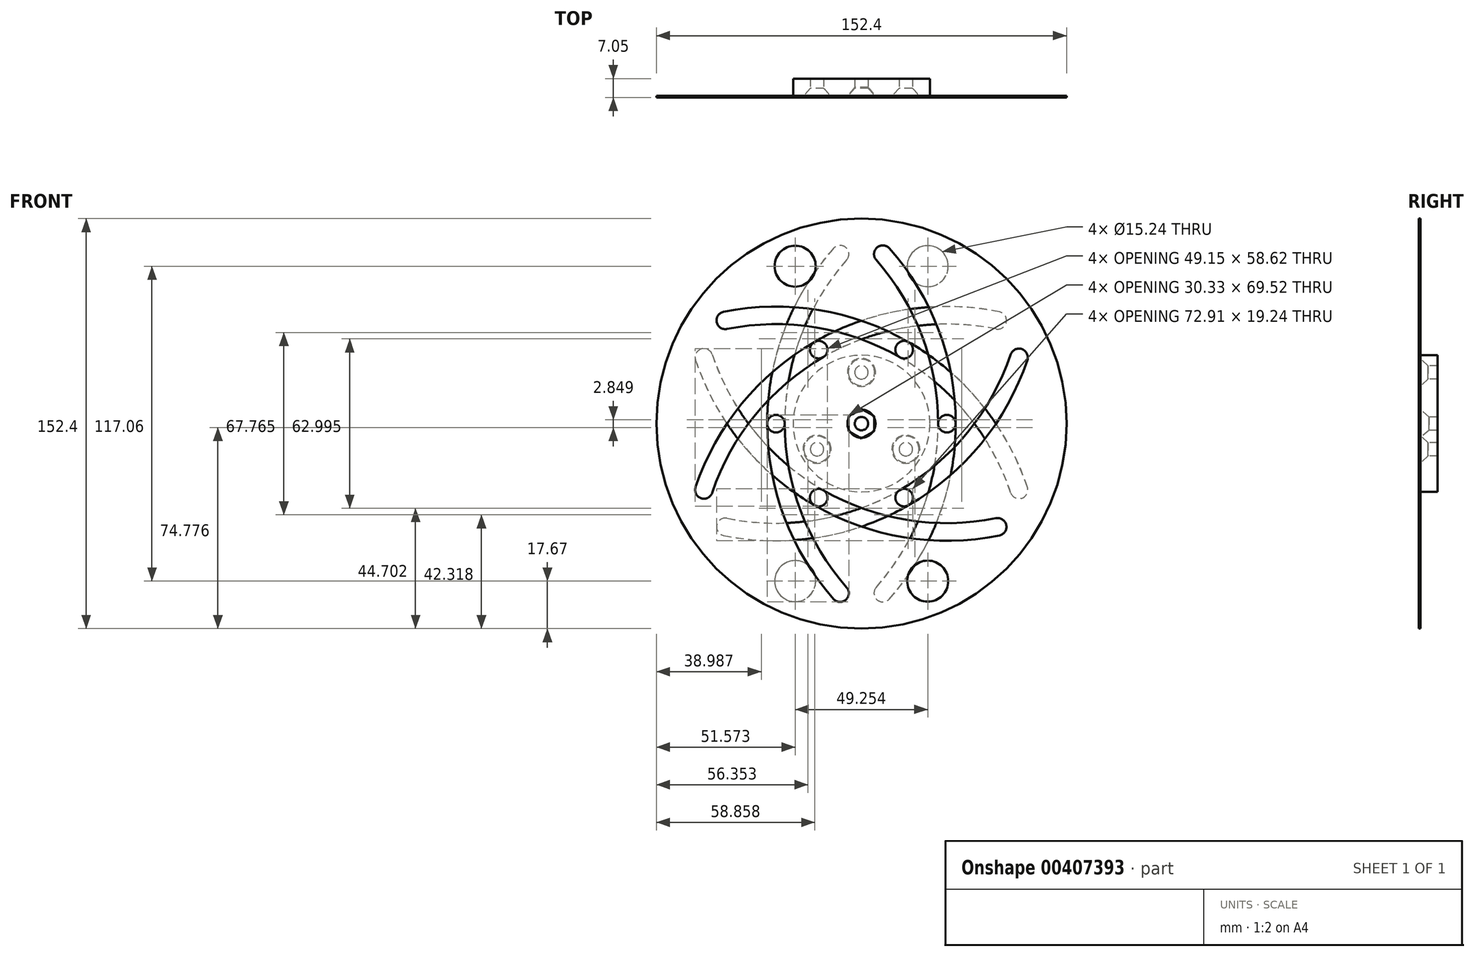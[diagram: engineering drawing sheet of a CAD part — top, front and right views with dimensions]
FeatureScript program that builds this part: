
annotation { "Feature Type Name" : "Feature", "Feature Type Description" : "" }
export const myFeature = defineFeature(function(context is Context, id is Id, definition is map)
    precondition{}
    {
        {
            assignVariable(context, id + "F0", {"name" : "plateThickness", "anyValue" : 0.35});
        }
        {
            var Q0;
            Q0=qCreatedBy(makeId("Front.planeOp"),FACE);
            var sketch = newSketch(context, id + "F1", { "sketchPlane" : qUnion([Q0])});
            skCircle(sketch, "E0", {"center": v(0, 0) * mm, "radius": 76.2 * mm});
            skLineSegment(sketch, "E1", {"start": v(38.1, -66) * mm, "end": v(-38.1, 66) * mm, "construction": true});
            skLineSegment(sketch, "E2", {"start": v(-76.2, 0) * mm, "end": v(76.2, 0) * mm, "construction": true});
            skCircle(sketch, "E3", {"center": v(0, 0) * mm, "radius": 63.5 * mm, "construction": true});
            skCircle(sketch, "E4", {"center": v(0, 0) * mm, "radius": 31.75 * mm, "construction": true});
            skLineSegment(sketch, "E5", {"start": v(27.7, -15.53) * mm, "end": v(55.38, -31.06) * mm, "construction": true});
            skPoint(sketch, "E6", {"position": v(41.54, -23.3) * mm});
            skArc(sketch, "E7", {"start": v(58.53, 24.63) * mm, "mid": v(41.96, -5.33) * mm, "end": v(15.87, -27.5) * mm, "construction": true});
            skArc(sketch, "E8.0.startCap", {"start": v(55.44, 25.67) * mm, "mid": v(59.57, 27.72) * mm, "end": v(61.62, 23.59) * mm});
            skArc(sketch, "E8.0.endCap", {"start": v(17.5, -30.32) * mm, "mid": v(13.05, -29.13) * mm, "end": v(14.24, -24.67) * mm});
            skArc(sketch, "E8.0.left", {"start": v(61.62, 23.59) * mm, "mid": v(44.49, -7.4) * mm, "end": v(17.5, -30.32) * mm});
            skArc(sketch, "E8.0.right", {"start": v(55.44, 25.67) * mm, "mid": v(39.44, -3.26) * mm, "end": v(14.24, -24.67) * mm});
            skLineSegment(sketch, "E9", {"start": v(0, 0) * mm, "end": v(0, 76.2) * mm, "construction": true});
            skArc(sketch, "E10.1.0", {"start": v(10.39, 65.16) * mm, "mid": v(28.65, 34.83) * mm, "end": v(35.01, 0) * mm});
            skArc(sketch, "E10.1.1", {"start": v(5.49, 60.84) * mm, "mid": v(22.55, 32.52) * mm, "end": v(28.49, 0) * mm});
            skArc(sketch, "E10.1.2", {"start": v(35.01, 0) * mm, "mid": v(31.75, -3.26) * mm, "end": v(28.49, 0) * mm});
            skArc(sketch, "E10.1.3", {"start": v(5.49, 60.84) * mm, "mid": v(5.78, 65.45) * mm, "end": v(10.39, 65.16) * mm});
            skArc(sketch, "E10.2.0", {"start": v(-51.24, 41.57) * mm, "mid": v(-15.84, 42.23) * mm, "end": v(17.5, 30.32) * mm});
            skArc(sketch, "E10.2.1", {"start": v(-49.95, 35.18) * mm, "mid": v(-16.9, 35.79) * mm, "end": v(14.24, 24.67) * mm});
            skArc(sketch, "E10.2.2", {"start": v(17.5, 30.32) * mm, "mid": v(18.7, 25.86) * mm, "end": v(14.24, 24.67) * mm});
            skArc(sketch, "E10.2.3", {"start": v(-49.95, 35.18) * mm, "mid": v(-53.8, 37.73) * mm, "end": v(-51.24, 41.57) * mm});
            skArc(sketch, "E11.3.3.0", {"start": v(-61.62, -23.59) * mm, "mid": v(-44.49, 7.4) * mm, "end": v(-17.5, 30.32) * mm});
            skArc(sketch, "E11.4.3.0", {"start": v(-55.44, -25.67) * mm, "mid": v(-39.44, 3.26) * mm, "end": v(-14.24, 24.67) * mm});
            skArc(sketch, "E11.8.3.0", {"start": v(-17.5, 30.32) * mm, "mid": v(-13.05, 29.13) * mm, "end": v(-14.24, 24.67) * mm});
            skArc(sketch, "E11.12.3.0", {"start": v(-55.44, -25.67) * mm, "mid": v(-59.57, -27.72) * mm, "end": v(-61.62, -23.59) * mm});
            skArc(sketch, "E11.3.4.0", {"start": v(-10.39, -65.16) * mm, "mid": v(-28.65, -34.83) * mm, "end": v(-35.01, 0) * mm});
            skArc(sketch, "E11.4.4.0", {"start": v(-5.49, -60.84) * mm, "mid": v(-22.55, -32.52) * mm, "end": v(-28.49, 0) * mm});
            skArc(sketch, "E11.8.4.0", {"start": v(-35.01, 0) * mm, "mid": v(-31.75, 3.26) * mm, "end": v(-28.49, 0) * mm});
            skArc(sketch, "E11.12.4.0", {"start": v(-5.49, -60.84) * mm, "mid": v(-5.78, -65.45) * mm, "end": v(-10.39, -65.16) * mm});
            skArc(sketch, "E11.3.5.0", {"start": v(51.24, -41.57) * mm, "mid": v(15.84, -42.23) * mm, "end": v(-17.5, -30.32) * mm});
            skArc(sketch, "E11.4.5.0", {"start": v(49.95, -35.18) * mm, "mid": v(16.9, -35.79) * mm, "end": v(-14.24, -24.67) * mm});
            skArc(sketch, "E11.8.5.0", {"start": v(-17.5, -30.32) * mm, "mid": v(-18.7, -25.86) * mm, "end": v(-14.24, -24.67) * mm});
            skArc(sketch, "E11.12.5.0", {"start": v(49.95, -35.18) * mm, "mid": v(53.8, -37.73) * mm, "end": v(51.24, -41.57) * mm});
            skCircle(sketch, "E12", {"center": v(-24.63, 58.53) * mm, "radius": 7.62 * mm});
            skArc(sketch, "E13", {"start": v(7.94, 63) * mm, "mid": v(-24.63, 58.53) * mm, "end": v(-50.6, 38.38) * mm, "construction": true});
            skCircle(sketch, "E14.1.0", {"center": v(24.63, -58.53) * mm, "radius": 7.62 * mm});
            skSolve(sketch);
        }
        {
            var Q0;
            Q0=qSketchRegion(id+"F1",true);
            var Q1;
            Q1=makeQuery(id+"F1.imprint","IMPRINT",FACE,{"disambiguationData":[TD([[makeQuery(id+"F1.imprint","IMPRINT",EDGE,{"derivedFrom":sQuery(id+"F1.wireOp",EDGE,"b587f6b5-7a6a-44af-b427-4ee7b0e66231.0")}),1.0]])]});
            var Q2;
            Q2=makeQuery(id+"F1.imprint","IMPRINT",FACE,{"disambiguationData":[TD([[makeQuery(id+"F1.imprint","IMPRINT",EDGE,{"derivedFrom":sQuery(id+"F1.wireOp",EDGE,"vc4YVOHs-SVUY-lYLu-5kIK-RnGjNBiSBPxz")}),-1.0]])]});
            extrude(context, id + "F2", {"entities" : qUnion([Q0, Q1, Q2]), "depth" : (getVariable(context, 'plateThickness')) * mm, "offsetDistance" : 25.4 * mm});
        }
        {
            var Q0;
            Q0=makeQuery(id+"F1.imprint","IMPRINT",FACE,{"disambiguationData":[TD([[makeQuery(id+"F1.imprint","IMPRINT",EDGE,{"derivedFrom":sQuery(id+"F1.wireOp",EDGE,"E0")}),1.0]])]});
            var Q1;
            Q1=makeQuery(id+"F2.opExtrude","CAP_FACE",FACE,{"disambiguationData":[OSD([sQuery(id+"F1.wireOp",EDGE,"E0"),sQuery(id+"F1.wireOp",EDGE,"E8.0.startCap"),sQuery(id+"F1.wireOp",EDGE,"E8.0.endCap"),sQuery(id+"F1.wireOp",EDGE,"E8.0.left"),sQuery(id+"F1.wireOp",EDGE,"E8.0.right"),sQuery(id+"F1.wireOp",EDGE,"9beebe2f-deec-4e0b-bc73-9199ee26bee9.1.0"),sQuery(id+"F1.wireOp",EDGE,"9beebe2f-deec-4e0b-bc73-9199ee26bee9.1.1"),sQuery(id+"F1.wireOp",EDGE,"9beebe2f-deec-4e0b-bc73-9199ee26bee9.1.2"),sQuery(id+"F1.wireOp",EDGE,"9beebe2f-deec-4e0b-bc73-9199ee26bee9.1.3"),sQuery(id+"F1.wireOp",EDGE,"9beebe2f-deec-4e0b-bc73-9199ee26bee9.2.0"),sQuery(id+"F1.wireOp",EDGE,"9beebe2f-deec-4e0b-bc73-9199ee26bee9.2.1"),sQuery(id+"F1.wireOp",EDGE,"9beebe2f-deec-4e0b-bc73-9199ee26bee9.2.2"),sQuery(id+"F1.wireOp",EDGE,"9beebe2f-deec-4e0b-bc73-9199ee26bee9.2.3"),sQuery(id+"F1.wireOp",EDGE,"9beebe2f-deec-4e0b-bc73-9199ee26bee9.3.0"),sQuery(id+"F1.wireOp",EDGE,"9beebe2f-deec-4e0b-bc73-9199ee26bee9.3.1"),sQuery(id+"F1.wireOp",EDGE,"9beebe2f-deec-4e0b-bc73-9199ee26bee9.3.2"),sQuery(id+"F1.wireOp",EDGE,"9beebe2f-deec-4e0b-bc73-9199ee26bee9.3.3"),sQuery(id+"F1.wireOp",EDGE,"9beebe2f-deec-4e0b-bc73-9199ee26bee9.4.0"),sQuery(id+"F1.wireOp",EDGE,"9beebe2f-deec-4e0b-bc73-9199ee26bee9.4.1"),sQuery(id+"F1.wireOp",EDGE,"9beebe2f-deec-4e0b-bc73-9199ee26bee9.4.2"),sQuery(id+"F1.wireOp",EDGE,"9beebe2f-deec-4e0b-bc73-9199ee26bee9.4.3"),sQuery(id+"F1.wireOp",EDGE,"9beebe2f-deec-4e0b-bc73-9199ee26bee9.5.0"),sQuery(id+"F1.wireOp",EDGE,"9beebe2f-deec-4e0b-bc73-9199ee26bee9.5.1"),sQuery(id+"F1.wireOp",EDGE,"9beebe2f-deec-4e0b-bc73-9199ee26bee9.5.2"),sQuery(id+"F1.wireOp",EDGE,"9beebe2f-deec-4e0b-bc73-9199ee26bee9.5.3"),sQuery(id+"F1.wireOp",EDGE,"b587f6b5-7a6a-44af-b427-4ee7b0e66231.0"),sQuery(id+"F1.wireOp",EDGE,"b587f6b5-7a6a-44af-b427-4ee7b0e66231.1"),sQuery(id+"F1.wireOp",EDGE,"b587f6b5-7a6a-44af-b427-4ee7b0e66231.2"),sQuery(id+"F1.wireOp",EDGE,"b587f6b5-7a6a-44af-b427-4ee7b0e66231.3"),sQuery(id+"F1.wireOp",EDGE,"b587f6b5-7a6a-44af-b427-4ee7b0e66231.4"),sQuery(id+"F1.wireOp",EDGE,"b587f6b5-7a6a-44af-b427-4ee7b0e66231.5")])],"isStart":false});
            extrude(context, id + "F3", {"entities" : qUnion([Q0]), "endBound" : BoundingType.UP_TO_SURFACE, "endBoundEntityFace" : qUnion([Q1]), "depth" : 25.4 * mm});
        }
        {
            var Q0;
            Q0=makeQuery(id+"F3.opExtrude","SWEPT_BODY",BODY,{"disambiguationData":[OSD([sQuery(id+"F1.wireOp",EDGE,"E0"),sQuery(id+"F1.wireOp",EDGE,"E8.0.startCap"),sQuery(id+"F1.wireOp",EDGE,"E8.0.endCap"),sQuery(id+"F1.wireOp",EDGE,"E8.0.left"),sQuery(id+"F1.wireOp",EDGE,"E8.0.right"),sQuery(id+"F1.wireOp",EDGE,"9beebe2f-deec-4e0b-bc73-9199ee26bee9.1.0"),sQuery(id+"F1.wireOp",EDGE,"9beebe2f-deec-4e0b-bc73-9199ee26bee9.1.1"),sQuery(id+"F1.wireOp",EDGE,"9beebe2f-deec-4e0b-bc73-9199ee26bee9.1.2"),sQuery(id+"F1.wireOp",EDGE,"9beebe2f-deec-4e0b-bc73-9199ee26bee9.1.3"),sQuery(id+"F1.wireOp",EDGE,"9beebe2f-deec-4e0b-bc73-9199ee26bee9.2.0"),sQuery(id+"F1.wireOp",EDGE,"9beebe2f-deec-4e0b-bc73-9199ee26bee9.2.1"),sQuery(id+"F1.wireOp",EDGE,"9beebe2f-deec-4e0b-bc73-9199ee26bee9.2.2"),sQuery(id+"F1.wireOp",EDGE,"9beebe2f-deec-4e0b-bc73-9199ee26bee9.2.3"),sQuery(id+"F1.wireOp",EDGE,"9beebe2f-deec-4e0b-bc73-9199ee26bee9.3.0"),sQuery(id+"F1.wireOp",EDGE,"9beebe2f-deec-4e0b-bc73-9199ee26bee9.3.1"),sQuery(id+"F1.wireOp",EDGE,"9beebe2f-deec-4e0b-bc73-9199ee26bee9.3.2"),sQuery(id+"F1.wireOp",EDGE,"9beebe2f-deec-4e0b-bc73-9199ee26bee9.3.3"),sQuery(id+"F1.wireOp",EDGE,"9beebe2f-deec-4e0b-bc73-9199ee26bee9.4.0"),sQuery(id+"F1.wireOp",EDGE,"9beebe2f-deec-4e0b-bc73-9199ee26bee9.4.1"),sQuery(id+"F1.wireOp",EDGE,"9beebe2f-deec-4e0b-bc73-9199ee26bee9.4.2"),sQuery(id+"F1.wireOp",EDGE,"9beebe2f-deec-4e0b-bc73-9199ee26bee9.4.3"),sQuery(id+"F1.wireOp",EDGE,"9beebe2f-deec-4e0b-bc73-9199ee26bee9.5.0"),sQuery(id+"F1.wireOp",EDGE,"9beebe2f-deec-4e0b-bc73-9199ee26bee9.5.1"),sQuery(id+"F1.wireOp",EDGE,"9beebe2f-deec-4e0b-bc73-9199ee26bee9.5.2"),sQuery(id+"F1.wireOp",EDGE,"9beebe2f-deec-4e0b-bc73-9199ee26bee9.5.3"),sQuery(id+"F1.wireOp",EDGE,"bZYdzHVk-sqhN-pvqg-Ma4H-s01bYcmrYiZ1")])]});
            var Q1;
            Q1=sQuery(id+"F1.wireOp",EDGE,"E9");
            transform(context, id + "F4", {"entities" : qUnion([Q0]), "transformType" : TransformType.ROTATION, "transformAxis" : qUnion([Q1]), "angle" : 180 * degree, "makeCopy" : false});
        }
        {
            var Q0;
            Q0=makeQuery(id+"F2.opExtrude","CAP_FACE",FACE,{"disambiguationData":[OSD([sQuery(id+"F1.wireOp",EDGE,"E0"),sQuery(id+"F1.wireOp",EDGE,"E8.0.startCap"),sQuery(id+"F1.wireOp",EDGE,"E8.0.endCap"),sQuery(id+"F1.wireOp",EDGE,"E8.0.left"),sQuery(id+"F1.wireOp",EDGE,"E8.0.right"),sQuery(id+"F1.wireOp",EDGE,"9beebe2f-deec-4e0b-bc73-9199ee26bee9.1.0"),sQuery(id+"F1.wireOp",EDGE,"9beebe2f-deec-4e0b-bc73-9199ee26bee9.1.1"),sQuery(id+"F1.wireOp",EDGE,"9beebe2f-deec-4e0b-bc73-9199ee26bee9.1.2"),sQuery(id+"F1.wireOp",EDGE,"9beebe2f-deec-4e0b-bc73-9199ee26bee9.1.3"),sQuery(id+"F1.wireOp",EDGE,"9beebe2f-deec-4e0b-bc73-9199ee26bee9.2.0"),sQuery(id+"F1.wireOp",EDGE,"9beebe2f-deec-4e0b-bc73-9199ee26bee9.2.1"),sQuery(id+"F1.wireOp",EDGE,"9beebe2f-deec-4e0b-bc73-9199ee26bee9.2.2"),sQuery(id+"F1.wireOp",EDGE,"9beebe2f-deec-4e0b-bc73-9199ee26bee9.2.3"),sQuery(id+"F1.wireOp",EDGE,"9beebe2f-deec-4e0b-bc73-9199ee26bee9.3.0"),sQuery(id+"F1.wireOp",EDGE,"9beebe2f-deec-4e0b-bc73-9199ee26bee9.3.1"),sQuery(id+"F1.wireOp",EDGE,"9beebe2f-deec-4e0b-bc73-9199ee26bee9.3.2"),sQuery(id+"F1.wireOp",EDGE,"9beebe2f-deec-4e0b-bc73-9199ee26bee9.3.3"),sQuery(id+"F1.wireOp",EDGE,"9beebe2f-deec-4e0b-bc73-9199ee26bee9.4.0"),sQuery(id+"F1.wireOp",EDGE,"9beebe2f-deec-4e0b-bc73-9199ee26bee9.4.1"),sQuery(id+"F1.wireOp",EDGE,"9beebe2f-deec-4e0b-bc73-9199ee26bee9.4.2"),sQuery(id+"F1.wireOp",EDGE,"9beebe2f-deec-4e0b-bc73-9199ee26bee9.4.3"),sQuery(id+"F1.wireOp",EDGE,"9beebe2f-deec-4e0b-bc73-9199ee26bee9.5.0"),sQuery(id+"F1.wireOp",EDGE,"9beebe2f-deec-4e0b-bc73-9199ee26bee9.5.1"),sQuery(id+"F1.wireOp",EDGE,"9beebe2f-deec-4e0b-bc73-9199ee26bee9.5.2"),sQuery(id+"F1.wireOp",EDGE,"9beebe2f-deec-4e0b-bc73-9199ee26bee9.5.3")])],"isStart":false});
            var sketch = newSketch(context, id + "F5", { "sketchPlane" : qUnion([Q0])});
            skPoint(sketch, "E15", {"position": v(0, 0) * mm});
            skSolve(sketch);
        }
        {
            var Q0;
            Q0=sQuery(id+"F5.wireOp",VERTEX,"E15");
            var Q1;
            Q1=makeQuery(id+"F2.opExtrude","SWEPT_BODY",BODY,{"disambiguationData":[OSD([sQuery(id+"F1.wireOp",EDGE,"E0"),sQuery(id+"F1.wireOp",EDGE,"E8.0.startCap"),sQuery(id+"F1.wireOp",EDGE,"E8.0.endCap"),sQuery(id+"F1.wireOp",EDGE,"E8.0.left"),sQuery(id+"F1.wireOp",EDGE,"E8.0.right"),sQuery(id+"F1.wireOp",EDGE,"9beebe2f-deec-4e0b-bc73-9199ee26bee9.1.0"),sQuery(id+"F1.wireOp",EDGE,"9beebe2f-deec-4e0b-bc73-9199ee26bee9.1.1"),sQuery(id+"F1.wireOp",EDGE,"9beebe2f-deec-4e0b-bc73-9199ee26bee9.1.2"),sQuery(id+"F1.wireOp",EDGE,"9beebe2f-deec-4e0b-bc73-9199ee26bee9.1.3"),sQuery(id+"F1.wireOp",EDGE,"9beebe2f-deec-4e0b-bc73-9199ee26bee9.2.0"),sQuery(id+"F1.wireOp",EDGE,"9beebe2f-deec-4e0b-bc73-9199ee26bee9.2.1"),sQuery(id+"F1.wireOp",EDGE,"9beebe2f-deec-4e0b-bc73-9199ee26bee9.2.2"),sQuery(id+"F1.wireOp",EDGE,"9beebe2f-deec-4e0b-bc73-9199ee26bee9.2.3"),sQuery(id+"F1.wireOp",EDGE,"9beebe2f-deec-4e0b-bc73-9199ee26bee9.3.0"),sQuery(id+"F1.wireOp",EDGE,"9beebe2f-deec-4e0b-bc73-9199ee26bee9.3.1"),sQuery(id+"F1.wireOp",EDGE,"9beebe2f-deec-4e0b-bc73-9199ee26bee9.3.2"),sQuery(id+"F1.wireOp",EDGE,"9beebe2f-deec-4e0b-bc73-9199ee26bee9.3.3"),sQuery(id+"F1.wireOp",EDGE,"9beebe2f-deec-4e0b-bc73-9199ee26bee9.4.0"),sQuery(id+"F1.wireOp",EDGE,"9beebe2f-deec-4e0b-bc73-9199ee26bee9.4.1"),sQuery(id+"F1.wireOp",EDGE,"9beebe2f-deec-4e0b-bc73-9199ee26bee9.4.2"),sQuery(id+"F1.wireOp",EDGE,"9beebe2f-deec-4e0b-bc73-9199ee26bee9.4.3"),sQuery(id+"F1.wireOp",EDGE,"9beebe2f-deec-4e0b-bc73-9199ee26bee9.5.0"),sQuery(id+"F1.wireOp",EDGE,"9beebe2f-deec-4e0b-bc73-9199ee26bee9.5.1"),sQuery(id+"F1.wireOp",EDGE,"9beebe2f-deec-4e0b-bc73-9199ee26bee9.5.2"),sQuery(id+"F1.wireOp",EDGE,"9beebe2f-deec-4e0b-bc73-9199ee26bee9.5.3")])]});
            hole(context, id + "F6", {"style" : HoleStyle.C_SINK, "endStyle" : HoleEndStyle.THROUGH, "standardTappedOrClearance" : lookupTablePath({ "standard" : "ANSI", "fit" : "Close", "size" : "#10", "type" : "Clearance" }), "standardBlindInLast" : lookupTablePath({ "fit" : "Close", "standard" : "ANSI", "size" : "#10", "type" : "Clearance" }), "holeDiameter" : 4.98 * mm, "cSinkDiameter" : 10.44 * mm, "cSinkAngle" : 82 * degree, "isTappedThrough" : true, "tappedDepth" : 12.7 * mm, "tapClearance" : 3, "locations" : qUnion([Q0]), "scope" : qUnion([Q1])});
        }
        {
            var Q0;
            Q0=sQuery(id+"F1.wireOp",VERTEX,"E0.center");
            var Q1;
            Q1=makeQuery(id+"F3.opExtrude","SWEPT_BODY",BODY,{"disambiguationData":[OSD([sQuery(id+"F1.wireOp",EDGE,"E0"),sQuery(id+"F1.wireOp",EDGE,"E8.0.startCap"),sQuery(id+"F1.wireOp",EDGE,"E8.0.endCap"),sQuery(id+"F1.wireOp",EDGE,"E8.0.left"),sQuery(id+"F1.wireOp",EDGE,"E8.0.right"),sQuery(id+"F1.wireOp",EDGE,"9beebe2f-deec-4e0b-bc73-9199ee26bee9.1.0"),sQuery(id+"F1.wireOp",EDGE,"9beebe2f-deec-4e0b-bc73-9199ee26bee9.1.1"),sQuery(id+"F1.wireOp",EDGE,"9beebe2f-deec-4e0b-bc73-9199ee26bee9.1.2"),sQuery(id+"F1.wireOp",EDGE,"9beebe2f-deec-4e0b-bc73-9199ee26bee9.1.3"),sQuery(id+"F1.wireOp",EDGE,"9beebe2f-deec-4e0b-bc73-9199ee26bee9.2.0"),sQuery(id+"F1.wireOp",EDGE,"9beebe2f-deec-4e0b-bc73-9199ee26bee9.2.1"),sQuery(id+"F1.wireOp",EDGE,"9beebe2f-deec-4e0b-bc73-9199ee26bee9.2.2"),sQuery(id+"F1.wireOp",EDGE,"9beebe2f-deec-4e0b-bc73-9199ee26bee9.2.3"),sQuery(id+"F1.wireOp",EDGE,"9beebe2f-deec-4e0b-bc73-9199ee26bee9.3.0"),sQuery(id+"F1.wireOp",EDGE,"9beebe2f-deec-4e0b-bc73-9199ee26bee9.3.1"),sQuery(id+"F1.wireOp",EDGE,"9beebe2f-deec-4e0b-bc73-9199ee26bee9.3.2"),sQuery(id+"F1.wireOp",EDGE,"9beebe2f-deec-4e0b-bc73-9199ee26bee9.3.3"),sQuery(id+"F1.wireOp",EDGE,"9beebe2f-deec-4e0b-bc73-9199ee26bee9.4.0"),sQuery(id+"F1.wireOp",EDGE,"9beebe2f-deec-4e0b-bc73-9199ee26bee9.4.1"),sQuery(id+"F1.wireOp",EDGE,"9beebe2f-deec-4e0b-bc73-9199ee26bee9.4.2"),sQuery(id+"F1.wireOp",EDGE,"9beebe2f-deec-4e0b-bc73-9199ee26bee9.4.3"),sQuery(id+"F1.wireOp",EDGE,"9beebe2f-deec-4e0b-bc73-9199ee26bee9.5.0"),sQuery(id+"F1.wireOp",EDGE,"9beebe2f-deec-4e0b-bc73-9199ee26bee9.5.1"),sQuery(id+"F1.wireOp",EDGE,"9beebe2f-deec-4e0b-bc73-9199ee26bee9.5.2"),sQuery(id+"F1.wireOp",EDGE,"9beebe2f-deec-4e0b-bc73-9199ee26bee9.5.3")])]});
            hole(context, id + "F7", {"style" : HoleStyle.SIMPLE, "endStyle" : HoleEndStyle.THROUGH, "standardTappedOrClearance" : lookupTablePath({ "standard" : "ANSI", "engagement" : "75%", "pitch" : "32 tpi", "size" : "#10", "type" : "Tapped" }), "standardBlindInLast" : lookupTablePath({ "standard" : "ANSI", "engagement" : "75%", "pitch" : "32 tpi", "size" : "#10", "type" : "Tapped" }), "holeDiameter" : 4.04 * mm, "showTappedDepth" : true, "isTappedThrough" : true, "tappedDepth" : 12.7 * mm, "tapClearance" : 3, "locations" : qUnion([Q0]), "scope" : qUnion([Q1]), "majorDiameter" : 4.83 * mm});
        }
        {
            var Q0;
            Q0=makeQuery(id+"F3.opExtrude","CAP_FACE",FACE,{"disambiguationData":[OSD([sQuery(id+"F1.wireOp",EDGE,"E0"),sQuery(id+"F1.wireOp",EDGE,"E8.0.startCap"),sQuery(id+"F1.wireOp",EDGE,"E8.0.endCap"),sQuery(id+"F1.wireOp",EDGE,"E8.0.left"),sQuery(id+"F1.wireOp",EDGE,"E8.0.right"),sQuery(id+"F1.wireOp",EDGE,"9beebe2f-deec-4e0b-bc73-9199ee26bee9.1.0"),sQuery(id+"F1.wireOp",EDGE,"9beebe2f-deec-4e0b-bc73-9199ee26bee9.1.1"),sQuery(id+"F1.wireOp",EDGE,"9beebe2f-deec-4e0b-bc73-9199ee26bee9.1.2"),sQuery(id+"F1.wireOp",EDGE,"9beebe2f-deec-4e0b-bc73-9199ee26bee9.1.3"),sQuery(id+"F1.wireOp",EDGE,"9beebe2f-deec-4e0b-bc73-9199ee26bee9.2.0"),sQuery(id+"F1.wireOp",EDGE,"9beebe2f-deec-4e0b-bc73-9199ee26bee9.2.1"),sQuery(id+"F1.wireOp",EDGE,"9beebe2f-deec-4e0b-bc73-9199ee26bee9.2.2"),sQuery(id+"F1.wireOp",EDGE,"9beebe2f-deec-4e0b-bc73-9199ee26bee9.2.3"),sQuery(id+"F1.wireOp",EDGE,"9beebe2f-deec-4e0b-bc73-9199ee26bee9.3.0"),sQuery(id+"F1.wireOp",EDGE,"9beebe2f-deec-4e0b-bc73-9199ee26bee9.3.1"),sQuery(id+"F1.wireOp",EDGE,"9beebe2f-deec-4e0b-bc73-9199ee26bee9.3.2"),sQuery(id+"F1.wireOp",EDGE,"9beebe2f-deec-4e0b-bc73-9199ee26bee9.3.3"),sQuery(id+"F1.wireOp",EDGE,"9beebe2f-deec-4e0b-bc73-9199ee26bee9.4.0"),sQuery(id+"F1.wireOp",EDGE,"9beebe2f-deec-4e0b-bc73-9199ee26bee9.4.1"),sQuery(id+"F1.wireOp",EDGE,"9beebe2f-deec-4e0b-bc73-9199ee26bee9.4.2"),sQuery(id+"F1.wireOp",EDGE,"9beebe2f-deec-4e0b-bc73-9199ee26bee9.4.3"),sQuery(id+"F1.wireOp",EDGE,"9beebe2f-deec-4e0b-bc73-9199ee26bee9.5.0"),sQuery(id+"F1.wireOp",EDGE,"9beebe2f-deec-4e0b-bc73-9199ee26bee9.5.1"),sQuery(id+"F1.wireOp",EDGE,"9beebe2f-deec-4e0b-bc73-9199ee26bee9.5.2"),sQuery(id+"F1.wireOp",EDGE,"9beebe2f-deec-4e0b-bc73-9199ee26bee9.5.3")])],"isStart":false});
            var sketch = newSketch(context, id + "F8", { "sketchPlane" : qUnion([Q0])});
            skCircle(sketch, "E16", {"center": v(0, 0) * mm, "radius": 25.4 * mm});
            skSolve(sketch);
        }
        {
            var Q0;
            Q0=qSketchRegion(id+"F8",true);
            extrude(context, id + "F9", {"entities" : qUnion([Q0]), "depth" : 6.35 * mm, "offsetDistance" : 25.4 * mm});
        }
        {
            var Q0;
            Q0=sQuery(id+"F8.wireOp",VERTEX,"E16.center");
            var Q1;
            Q1=makeQuery(id+"F9.opExtrude","SWEPT_BODY",BODY,{"disambiguationData":[OSD([sQuery(id+"F8.wireOp",EDGE,"E16")])]});
            hole(context, id + "F10", {"style" : HoleStyle.C_SINK, "endStyle" : HoleEndStyle.THROUGH, "oppositeDirection" : true, "standardTappedOrClearance" : lookupTablePath({ "standard" : "ANSI", "fit" : "Close", "size" : "#10", "type" : "Clearance" }), "standardBlindInLast" : lookupTablePath({ "fit" : "Close", "standard" : "ANSI", "size" : "#10", "type" : "Clearance" }), "holeDiameter" : 4.98 * mm, "cSinkDiameter" : 10.44 * mm, "cSinkAngle" : 82 * degree, "isTappedThrough" : true, "tappedDepth" : 12.7 * mm, "tapClearance" : 3, "locations" : qUnion([Q0]), "scope" : qUnion([Q1])});
        }
        {
            var Q0;
            Q0=makeQuery(id+"F3.opExtrude","CAP_FACE",FACE,{"disambiguationData":[OSD([sQuery(id+"F1.wireOp",EDGE,"E0"),sQuery(id+"F1.wireOp",EDGE,"E8.0.startCap"),sQuery(id+"F1.wireOp",EDGE,"E8.0.endCap"),sQuery(id+"F1.wireOp",EDGE,"E8.0.left"),sQuery(id+"F1.wireOp",EDGE,"E8.0.right"),sQuery(id+"F1.wireOp",EDGE,"jn4Evwqn-haMm-BaYE-fIlN-nHzIOZhbmQ3t"),sQuery(id+"F1.wireOp",EDGE,"eef2ee24-f27b-465e-8981-fff5df70cd24.1.0"),sQuery(id+"F1.wireOp",EDGE,"eef2ee24-f27b-465e-8981-fff5df70cd24.1.1"),sQuery(id+"F1.wireOp",EDGE,"eef2ee24-f27b-465e-8981-fff5df70cd24.1.2"),sQuery(id+"F1.wireOp",EDGE,"eef2ee24-f27b-465e-8981-fff5df70cd24.1.3"),sQuery(id+"F1.wireOp",EDGE,"eef2ee24-f27b-465e-8981-fff5df70cd24.1.4"),sQuery(id+"F1.wireOp",EDGE,"eef2ee24-f27b-465e-8981-fff5df70cd24.2.0"),sQuery(id+"F1.wireOp",EDGE,"eef2ee24-f27b-465e-8981-fff5df70cd24.2.1"),sQuery(id+"F1.wireOp",EDGE,"eef2ee24-f27b-465e-8981-fff5df70cd24.2.2"),sQuery(id+"F1.wireOp",EDGE,"eef2ee24-f27b-465e-8981-fff5df70cd24.2.3"),sQuery(id+"F1.wireOp",EDGE,"eef2ee24-f27b-465e-8981-fff5df70cd24.2.4"),sQuery(id+"F1.wireOp",EDGE,"eef2ee24-f27b-465e-8981-fff5df70cd24.3.0"),sQuery(id+"F1.wireOp",EDGE,"eef2ee24-f27b-465e-8981-fff5df70cd24.3.1"),sQuery(id+"F1.wireOp",EDGE,"eef2ee24-f27b-465e-8981-fff5df70cd24.3.2"),sQuery(id+"F1.wireOp",EDGE,"eef2ee24-f27b-465e-8981-fff5df70cd24.3.3"),sQuery(id+"F1.wireOp",EDGE,"eef2ee24-f27b-465e-8981-fff5df70cd24.3.4"),sQuery(id+"F1.wireOp",EDGE,"eef2ee24-f27b-465e-8981-fff5df70cd24.4.0"),sQuery(id+"F1.wireOp",EDGE,"eef2ee24-f27b-465e-8981-fff5df70cd24.4.1"),sQuery(id+"F1.wireOp",EDGE,"eef2ee24-f27b-465e-8981-fff5df70cd24.4.2"),sQuery(id+"F1.wireOp",EDGE,"eef2ee24-f27b-465e-8981-fff5df70cd24.4.3"),sQuery(id+"F1.wireOp",EDGE,"eef2ee24-f27b-465e-8981-fff5df70cd24.4.4"),sQuery(id+"F1.wireOp",EDGE,"eef2ee24-f27b-465e-8981-fff5df70cd24.5.0"),sQuery(id+"F1.wireOp",EDGE,"eef2ee24-f27b-465e-8981-fff5df70cd24.5.1"),sQuery(id+"F1.wireOp",EDGE,"eef2ee24-f27b-465e-8981-fff5df70cd24.5.2"),sQuery(id+"F1.wireOp",EDGE,"eef2ee24-f27b-465e-8981-fff5df70cd24.5.3"),sQuery(id+"F1.wireOp",EDGE,"eef2ee24-f27b-465e-8981-fff5df70cd24.5.4")])],"isStart":true});
            var sketch = newSketch(context, id + "F11", { "sketchPlane" : qUnion([Q0])});
            skCircle(sketch, "E17", {"center": v(0, 0) * mm, "radius": 19.05 * mm, "construction": true});
            skPoint(sketch, "E18", {"position": v(0, 19.05) * mm});
            skPoint(sketch, "E19.1.0", {"position": v(-16.5, -9.53) * mm});
            skPoint(sketch, "E19.2.0", {"position": v(16.5, -9.52) * mm});
            skSolve(sketch);
        }
        {
            var Q0;
            Q0=sQuery(id+"F11.wireOp",VERTEX,"E18");
            var Q1;
            Q1=sQuery(id+"F11.wireOp",VERTEX,"E19.2.0");
            var Q2;
            Q2=sQuery(id+"F11.wireOp",VERTEX,"E19.1.0");
            var Q3;
            Q3=makeQuery(id+"F3.opExtrude","SWEPT_BODY",BODY,{"disambiguationData":[OSD([sQuery(id+"F1.wireOp",EDGE,"E0"),sQuery(id+"F1.wireOp",EDGE,"E8.0.startCap"),sQuery(id+"F1.wireOp",EDGE,"E8.0.endCap"),sQuery(id+"F1.wireOp",EDGE,"E8.0.left"),sQuery(id+"F1.wireOp",EDGE,"E8.0.right"),sQuery(id+"F1.wireOp",EDGE,"jn4Evwqn-haMm-BaYE-fIlN-nHzIOZhbmQ3t"),sQuery(id+"F1.wireOp",EDGE,"eef2ee24-f27b-465e-8981-fff5df70cd24.1.0"),sQuery(id+"F1.wireOp",EDGE,"eef2ee24-f27b-465e-8981-fff5df70cd24.1.1"),sQuery(id+"F1.wireOp",EDGE,"eef2ee24-f27b-465e-8981-fff5df70cd24.1.2"),sQuery(id+"F1.wireOp",EDGE,"eef2ee24-f27b-465e-8981-fff5df70cd24.1.3"),sQuery(id+"F1.wireOp",EDGE,"eef2ee24-f27b-465e-8981-fff5df70cd24.1.4"),sQuery(id+"F1.wireOp",EDGE,"eef2ee24-f27b-465e-8981-fff5df70cd24.2.0"),sQuery(id+"F1.wireOp",EDGE,"eef2ee24-f27b-465e-8981-fff5df70cd24.2.1"),sQuery(id+"F1.wireOp",EDGE,"eef2ee24-f27b-465e-8981-fff5df70cd24.2.2"),sQuery(id+"F1.wireOp",EDGE,"eef2ee24-f27b-465e-8981-fff5df70cd24.2.3"),sQuery(id+"F1.wireOp",EDGE,"eef2ee24-f27b-465e-8981-fff5df70cd24.2.4"),sQuery(id+"F1.wireOp",EDGE,"eef2ee24-f27b-465e-8981-fff5df70cd24.3.0"),sQuery(id+"F1.wireOp",EDGE,"eef2ee24-f27b-465e-8981-fff5df70cd24.3.1"),sQuery(id+"F1.wireOp",EDGE,"eef2ee24-f27b-465e-8981-fff5df70cd24.3.2"),sQuery(id+"F1.wireOp",EDGE,"eef2ee24-f27b-465e-8981-fff5df70cd24.3.3"),sQuery(id+"F1.wireOp",EDGE,"eef2ee24-f27b-465e-8981-fff5df70cd24.3.4"),sQuery(id+"F1.wireOp",EDGE,"eef2ee24-f27b-465e-8981-fff5df70cd24.4.0"),sQuery(id+"F1.wireOp",EDGE,"eef2ee24-f27b-465e-8981-fff5df70cd24.4.1"),sQuery(id+"F1.wireOp",EDGE,"eef2ee24-f27b-465e-8981-fff5df70cd24.4.2"),sQuery(id+"F1.wireOp",EDGE,"eef2ee24-f27b-465e-8981-fff5df70cd24.4.3"),sQuery(id+"F1.wireOp",EDGE,"eef2ee24-f27b-465e-8981-fff5df70cd24.4.4"),sQuery(id+"F1.wireOp",EDGE,"eef2ee24-f27b-465e-8981-fff5df70cd24.5.0"),sQuery(id+"F1.wireOp",EDGE,"eef2ee24-f27b-465e-8981-fff5df70cd24.5.1"),sQuery(id+"F1.wireOp",EDGE,"eef2ee24-f27b-465e-8981-fff5df70cd24.5.2"),sQuery(id+"F1.wireOp",EDGE,"eef2ee24-f27b-465e-8981-fff5df70cd24.5.3"),sQuery(id+"F1.wireOp",EDGE,"eef2ee24-f27b-465e-8981-fff5df70cd24.5.4")])]});
            var Q4;
            Q4=makeQuery(id+"F9.opExtrude","SWEPT_BODY",BODY,{"disambiguationData":[OSD([sQuery(id+"F8.wireOp",EDGE,"E16")])]});
            hole(context, id + "F12", {"style" : HoleStyle.C_SINK, "endStyle" : HoleEndStyle.THROUGH, "standardTappedOrClearance" : lookupTablePath({ "standard" : "ANSI", "fit" : "Close", "size" : "#10", "type" : "Clearance" }), "standardBlindInLast" : lookupTablePath({ "fit" : "Close", "standard" : "ANSI", "size" : "#10", "type" : "Clearance" }), "holeDiameter" : 4.98 * mm, "cSinkDiameter" : 10.44 * mm, "cSinkAngle" : 82 * degree, "isTappedThrough" : true, "tappedDepth" : 12.7 * mm, "tapClearance" : 3, "locations" : qUnion([Q0, Q1, Q2]), "scope" : qUnion([Q3, Q4])});
        }
        {
            var Q0;
            Q0=makeQuery(id+"F8.imprint","IMPRINT",FACE,{"disambiguationData":[TD([[makeQuery(id+"F8.imprint","IMPRINT",EDGE,{"derivedFrom":sQuery(id+"F8.wireOp",EDGE,"E16")}),-1.0]])]});
            var sketch = newSketch(context, id + "F13", { "sketchPlane" : qUnion([Q0])});
            skCircle(sketch, "E20.cCircle", {"center": v(0, 0) * mm, "radius": 4.76 * mm, "construction": true});
            skLineSegment(sketch, "E20.0", {"start": v(0, 5.5) * mm, "end": v(-4.76, 2.75) * mm});
            skLineSegment(sketch, "E20.1", {"start": v(4.76, 2.75) * mm, "end": v(0, 5.5) * mm});
            skLineSegment(sketch, "E20.2", {"start": v(4.76, -2.75) * mm, "end": v(4.76, 2.75) * mm});
            skLineSegment(sketch, "E20.3", {"start": v(0, -5.5) * mm, "end": v(4.76, -2.75) * mm});
            skLineSegment(sketch, "E20.4", {"start": v(-4.76, -2.75) * mm, "end": v(0, -5.5) * mm});
            skLineSegment(sketch, "E20.5", {"start": v(-4.76, 2.75) * mm, "end": v(-4.76, -2.75) * mm});
            skPoint(sketch, "E20.0.midPoint", {"position": v(-2.38, 4.12) * mm});
            skSolve(sketch);
        }
        {
            var Q0;
            Q0=makeQuery(id+"F13.imprint","IMPRINT",FACE,{"disambiguationData":[TD([[makeQuery(id+"F13.imprint","IMPRINT",EDGE,{"derivedFrom":sQuery(id+"F13.wireOp",EDGE,"E20.0")}),1.0]])]});
            extrude(context, id + "F14", {"entities" : qUnion([Q0]), "operationType" : NewBodyOperationType.REMOVE, "endBound" : BoundingType.THROUGH_ALL, "oppositeDirection" : true, "depth" : 25.4 * mm, "offsetDistance" : 25.4 * mm});
        }
    });
